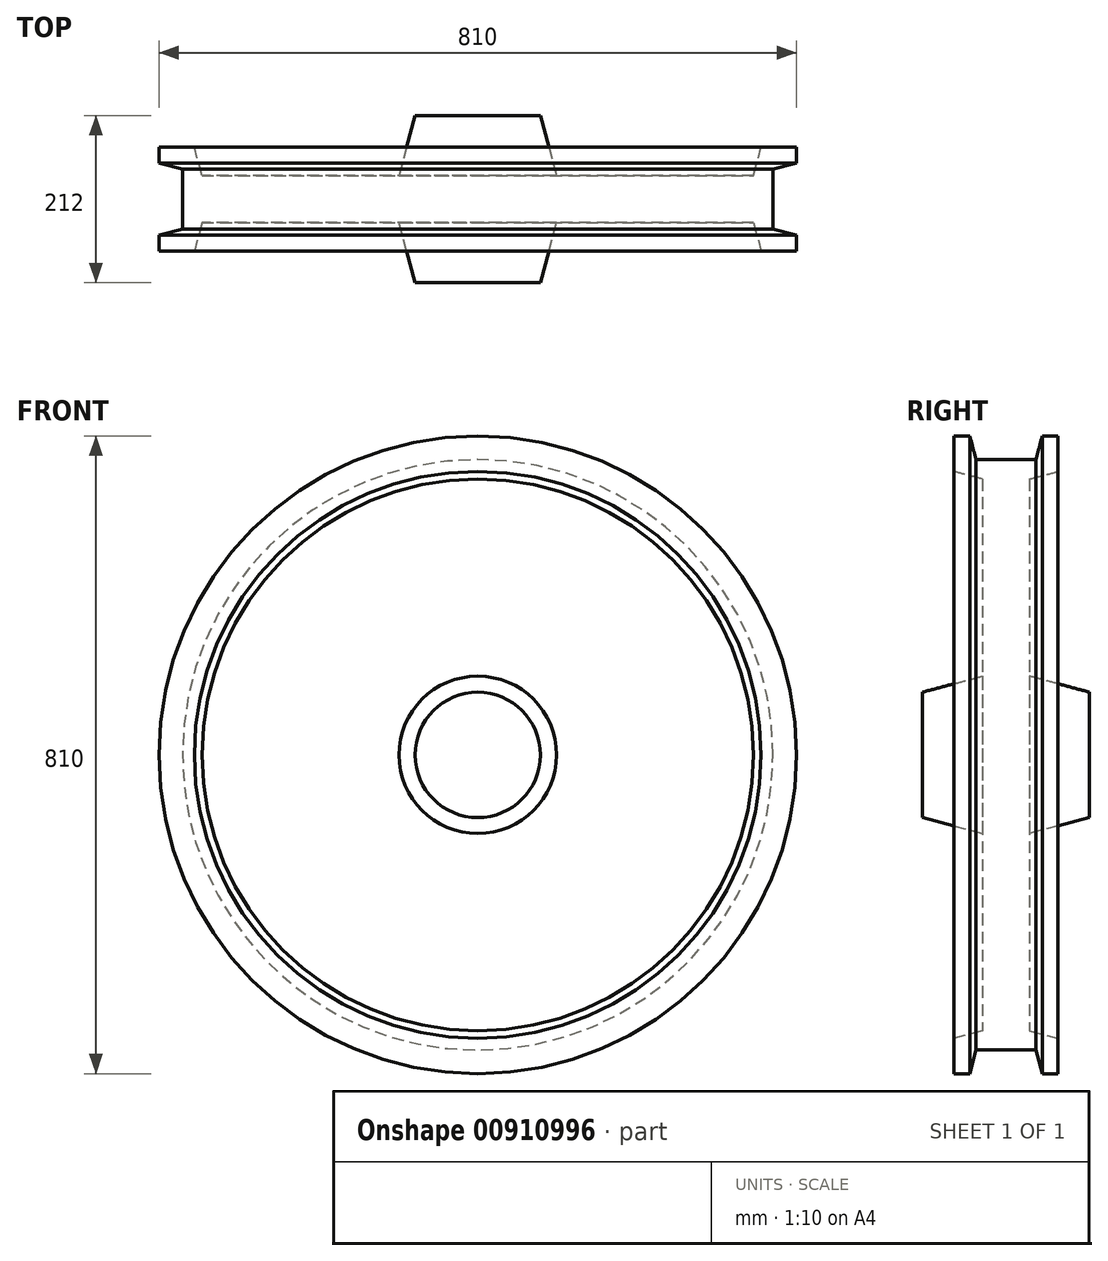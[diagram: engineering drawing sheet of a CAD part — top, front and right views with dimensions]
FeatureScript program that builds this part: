
annotation { "Feature Type Name" : "Feature", "Feature Type Description" : "" }
export const myFeature = defineFeature(function(context is Context, id is Id, definition is map)
    precondition{}
    {
        {
            var Q0;
            Q0=qCreatedBy(makeId("Front.planeOp"),FACE);
            var sketch = newSketch(context, id + "F0", { "sketchPlane" : qUnion([Q0])});
            skCircle(sketch, "E0", {"center": v(0, 0) * mm, "radius": 50 * mm});
            skSolve(sketch);
        }
        {
            var Q0;
            Q0=qCreatedBy(makeId("Right.planeOp"),FACE);
            var sketch = newSketch(context, id + "F1", { "sketchPlane" : qUnion([Q0])});
            skLineSegment(sketch, "E1", {"start": v(30, 0) * mm, "end": v(-30, 0) * mm});
            skLineSegment(sketch, "E2", {"start": v(30, 0) * mm, "end": v(30, 350.35) * mm});
            skLineSegment(sketch, "E3", {"start": v(0, 0) * mm, "end": v(0, 405) * mm, "construction": true});
            skLineSegment(sketch, "E4", {"start": v(0, 360) * mm, "end": v(66, 360) * mm, "construction": true});
            skLineSegment(sketch, "E5", {"start": v(66, 360) * mm, "end": v(66, 405) * mm});
            skLineSegment(sketch, "E6", {"start": v(66, 405) * mm, "end": v(46, 405) * mm});
            skLineSegment(sketch, "E7", {"start": v(66, 360) * mm, "end": v(30, 350.35) * mm});
            skLineSegment(sketch, "E8", {"start": v(46, 405) * mm, "end": v(46, 375) * mm, "construction": true});
            skLineSegment(sketch, "E9", {"start": v(37.96, 375) * mm, "end": v(0, 375) * mm});
            skLineSegment(sketch, "E10", {"start": v(46, 405) * mm, "end": v(37.96, 375) * mm});
            skLineSegment(sketch, "E11.MirrorCS", {"start": v(-37.96, 375) * mm, "end": v(0, 375) * mm});
            skLineSegment(sketch, "E12.MirrorCS", {"start": v(-46, 405) * mm, "end": v(-37.96, 375) * mm});
            skLineSegment(sketch, "E13.MirrorCS", {"start": v(-66, 405) * mm, "end": v(-46, 405) * mm});
            skLineSegment(sketch, "E14.MirrorCS", {"start": v(-66, 360) * mm, "end": v(-66, 405) * mm});
            skLineSegment(sketch, "E15.MirrorCS", {"start": v(-66, 360) * mm, "end": v(-30, 350.35) * mm});
            skLineSegment(sketch, "E16.MirrorCS", {"start": v(-30, 0) * mm, "end": v(-30, 350.35) * mm});
            skLineSegment(sketch, "E17.bottom", {"start": v(30, 0) * mm, "end": v(106, 0) * mm});
            skLineSegment(sketch, "E17.left", {"start": v(30, 0) * mm, "end": v(30, 100) * mm});
            skLineSegment(sketch, "E17.right", {"start": v(106, 0) * mm, "end": v(106, 79.64) * mm});
            skLineSegment(sketch, "E18", {"start": v(66, 375.2) * mm, "end": v(106, 375.2) * mm, "construction": true});
            skLineSegment(sketch, "E19", {"start": v(106, 79.64) * mm, "end": v(30, 100) * mm});
            skPoint(sketch, "E20.orphan", {"position": v(106, 100) * mm});
            skLineSegment(sketch, "E21.MirrorCS", {"start": v(-106, 79.64) * mm, "end": v(-30, 100) * mm});
            skLineSegment(sketch, "E22.MirrorCS", {"start": v(-106, 0) * mm, "end": v(-106, 79.64) * mm});
            skLineSegment(sketch, "E23.MirrorCS", {"start": v(-30, 0) * mm, "end": v(-106, 0) * mm});
            skLineSegment(sketch, "E24", {"start": v(106, 375.2) * mm, "end": v(106, 79.64) * mm, "construction": true});
            skLineSegment(sketch, "E25", {"start": v(106, 79.64) * mm, "end": v(0, 79.64) * mm, "construction": true});
            skSolve(sketch);
        }
        {
            var Q0;
            Q0 = qSketchRegion(id + "F1", true);
            var Q1;
            Q1=sQuery(id+"F0.wireOp",EDGE,"E0");
            revolve(context, id + "F2", {"surfaceOperationType" : NewSurfaceOperationType.NEW, "entities" : qUnion([Q0]), "axis" : qUnion([Q1]), "revolveType" : RevolveType.FULL});
        }
    });
